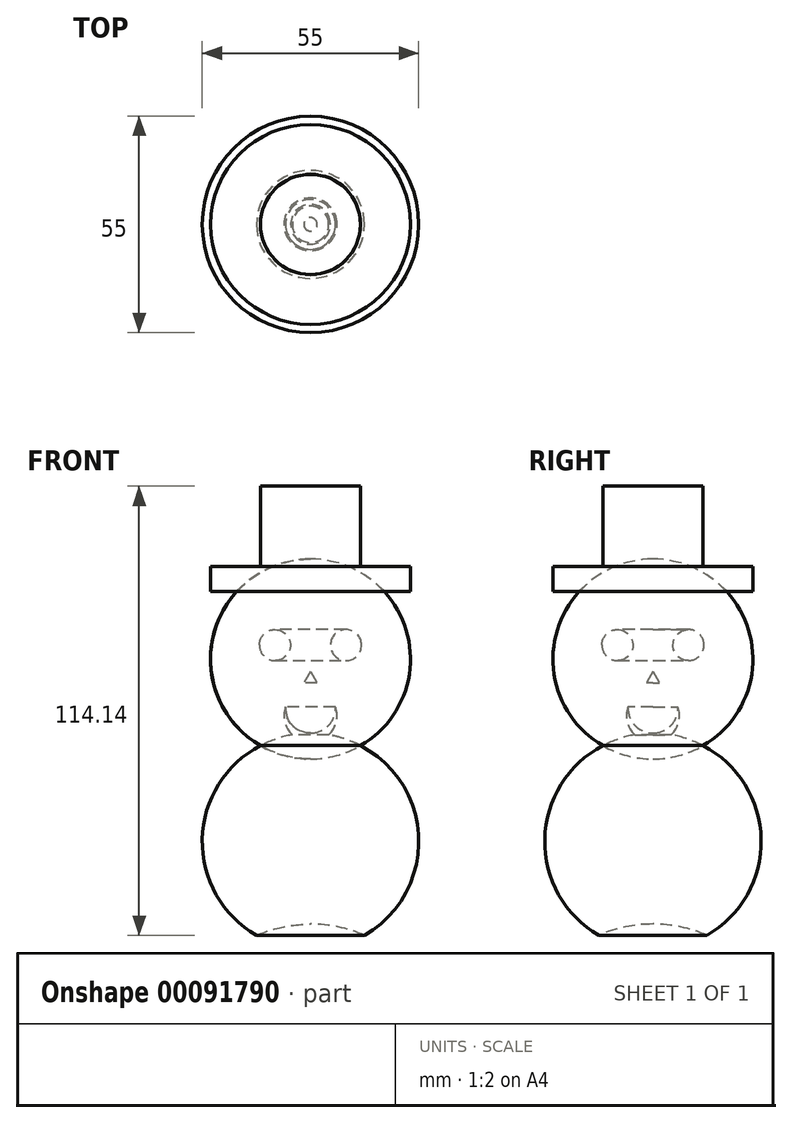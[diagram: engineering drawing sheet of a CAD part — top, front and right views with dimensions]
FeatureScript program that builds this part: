
annotation { "Feature Type Name" : "Feature", "Feature Type Description" : "" }
export const myFeature = defineFeature(function(context is Context, id is Id, definition is map)
    precondition{}
    {
        {
            var Q0;
            Q0=qCreatedBy(makeId("Front.planeOp"),FACE);
            var sketch = newSketch(context, id + "F0", { "sketchPlane" : qUnion([Q0])});
            skCircle(sketch, "E0", {"center": v(0, 0) * mm, "radius": 27.5 * mm});
            skCircle(sketch, "E1", {"center": v(0, 46.37) * mm, "radius": 25.4 * mm});
            skCircle(sketch, "E2", {"center": v(0, -55.26) * mm, "radius": 34.3 * mm});
            skCircle(sketch, "E3", {"center": v(-9.03, 49.92) * mm, "radius": 3.95 * mm});
            skCircle(sketch, "E4.MirrorC", {"center": v(9.03, 49.92) * mm, "radius": 3.95 * mm});
            skLineSegment(sketch, "E5", {"start": v(0, 43.2) * mm, "end": v(-1.7, 40.25) * mm});
            skLineSegment(sketch, "E6", {"start": v(-1.7, 40.25) * mm, "end": v(1.7, 40.25) * mm});
            skPoint(sketch, "E7.endSnap0", {"position": v(-0.85, 41.73) * mm});
            skLineSegment(sketch, "E8", {"start": v(0, 43.2) * mm, "end": v(1.7, 40.25) * mm});
            skArc(sketch, "E9", {"start": v(-6.34, 34.24) * mm, "mid": v(-4.6, 29.53) * mm, "end": v(0, 27.55) * mm});
            skArc(sketch, "E10", {"start": v(-6.34, 34.24) * mm, "mid": v(-5.5, 28.11) * mm, "end": v(0, 25.27) * mm});
            skArc(sketch, "E11.MirrorCS", {"start": v(6.34, 34.24) * mm, "mid": v(4.6, 29.53) * mm, "end": v(0, 27.55) * mm});
            skArc(sketch, "E12.MirrorCS", {"start": v(6.34, 34.24) * mm, "mid": v(5.5, 28.11) * mm, "end": v(0, 25.27) * mm});
            skLineSegment(sketch, "E13", {"start": v(0, 71.77) * mm, "end": v(0, -89.55) * mm});
            skSolve(sketch);
        }
        {
            var Q0;
            Q0=qCreatedBy(makeId("Front.planeOp"),FACE);
            var sketch = newSketch(context, id + "F1", { "sketchPlane" : qUnion([Q0])});
            skLineSegment(sketch, "E14.bottom", {"start": v(0, 69.85) * mm, "end": v(25.4, 69.85) * mm});
            skLineSegment(sketch, "E14.top", {"start": v(0, 63.5) * mm, "end": v(25.4, 63.5) * mm});
            skLineSegment(sketch, "E14.left", {"start": v(0, 69.85) * mm, "end": v(0, 63.5) * mm});
            skLineSegment(sketch, "E14.right", {"start": v(25.4, 69.85) * mm, "end": v(25.4, 63.5) * mm});
            skLineSegment(sketch, "E15.top", {"start": v(12.7, 90.3) * mm, "end": v(0, 90.3) * mm});
            skLineSegment(sketch, "E15.left", {"start": v(12.7, 69.85) * mm, "end": v(12.7, 90.3) * mm});
            skLineSegment(sketch, "E15.right", {"start": v(0, 69.85) * mm, "end": v(0, 90.3) * mm});
            skLineSegment(sketch, "E16.MirrorCS", {"start": v(-12.7, 90.3) * mm, "end": v(0, 90.3) * mm});
            skLineSegment(sketch, "E17.MirrorCS", {"start": v(-12.7, 69.85) * mm, "end": v(-12.7, 90.3) * mm});
            skLineSegment(sketch, "E18.MirrorCS", {"start": v(0, 63.5) * mm, "end": v(-25.4, 63.5) * mm});
            skLineSegment(sketch, "E19.MirrorCS", {"start": v(-25.4, 69.85) * mm, "end": v(-25.4, 63.5) * mm});
            skLineSegment(sketch, "E20.MirrorCS", {"start": v(0, 69.85) * mm, "end": v(-25.4, 69.85) * mm});
            skSolve(sketch);
        }
        {
            var Q0;
            Q0=makeQuery(id+"F0.imprint","IMPRINT",FACE,{"disambiguationData":[TD([[makeQuery(id+"F0.imprint","IMPRINT",EDGE,{"derivedFrom":sQuery(id+"F0.wireOp",EDGE,"E3")}),-1.0]])]});
            var Q1;
            {var subQ0=sQuery(id+"F0.wireOp",EDGE,"E1");var subQ1=sQuery(id+"F0.wireOp",EDGE,"E0");var subQ2=makeQuery(id+"F0.imprint","INTERSECT",VERTEX,{"disambiguationData":[OD(1.0)],"derivedFrom":[subQ1,subQ0]});Q1=makeQuery(id+"F0.imprint","IMPRINT",FACE,{"disambiguationData":[TD([[makeQuery(id+"F0.imprint","IMPRINT",EDGE,{"disambiguationData":[TD([[subQ2,-1.0]])],"derivedFrom":subQ1}),1.0]])]});}
            var Q2;
            {var subQ0=sQuery(id+"F0.wireOp",EDGE,"E2");var subQ1=sQuery(id+"F0.wireOp",EDGE,"E0");var subQ2=makeQuery(id+"F0.imprint","INTERSECT",VERTEX,{"disambiguationData":[OD(0.0)],"derivedFrom":[subQ1,subQ0]});Q2=makeQuery(id+"F0.imprint","IMPRINT",FACE,{"disambiguationData":[TD([[makeQuery(id+"F0.imprint","IMPRINT",EDGE,{"disambiguationData":[TD([[subQ2,-1.0]])],"derivedFrom":subQ1}),-1.0]])]});}
            var Q3;
            Q3=sQuery(id+"F0.wireOp",EDGE,"E3");
            var Q4;
            Q4=sQuery(id+"F0.wireOp",EDGE,"E1");
            var Q5;
            Q5=sQuery(id+"F0.wireOp",EDGE,"E0");
            var Q6;
            Q6=sQuery(id+"F0.wireOp",EDGE,"E10");
            var Q7;
            Q7=sQuery(id+"F0.wireOp",EDGE,"E9");
            var Q8;
            Q8=sQuery(id+"F0.wireOp",EDGE,"E5");
            var Q9;
            Q9=sQuery(id+"F0.wireOp",EDGE,"E6");
            var Q10;
            Q10=sQuery(id+"F0.wireOp",EDGE,"E2");
            var Q11;
            Q11=sQuery(id+"F0.wireOp",EDGE,"E13");
            revolve(context, id + "F2", {"entities" : qUnion([Q0, Q1, Q2]), "surfaceEntities" : qUnion([Q3, Q4, Q5, Q6, Q7, Q8, Q9, Q10]), "axis" : qUnion([Q11]), "revolveType" : RevolveType.FULL});
        }
        {
            var Q0;
            {var subQ0=sQuery(id+"F1.wireOp",EDGE,"E15.right");Q0=makeQuery(id+"F1.imprint","IMPRINT",FACE,{"disambiguationData":[TD([[makeQuery(id+"F1.imprint","IMPRINT",EDGE,{"derivedFrom":subQ0}),1.0]])]});}
            var Q1;
            {var subQ1=sQuery(id+"F1.wireOp",EDGE,"E14.left");Q1=makeQuery(id+"F1.imprint","IMPRINT",FACE,{"disambiguationData":[TD([[makeQuery(id+"F1.imprint","IMPRINT",EDGE,{"derivedFrom":subQ1}),-1.0]])]});}
            var Q2;
            Q2=sQuery(id+"F1.wireOp",EDGE,"E17.MirrorCS");
            var Q3;
            Q3=sQuery(id+"F1.wireOp",EDGE,"E20.MirrorCS");
            var Q4;
            Q4=sQuery(id+"F1.wireOp",EDGE,"E19.MirrorCS");
            var Q5;
            Q5=sQuery(id+"F1.wireOp",EDGE,"E18.MirrorCS");
            var Q6;
            Q6=sQuery(id+"F1.wireOp",EDGE,"E16.MirrorCS");
            var Q7;
            Q7=sQuery(id+"F1.wireOp",EDGE,"E14.left");
            revolve(context, id + "F3", {"entities" : qUnion([Q0, Q1]), "surfaceEntities" : qUnion([Q2, Q3, Q4, Q5, Q6]), "axis" : qUnion([Q7]), "revolveType" : RevolveType.FULL});
        }
        {
            var Q0;
            Q0=sQuery(id+"F0.wireOp",EDGE,"E3");
            var Q1;
            Q1=sQuery(id+"F0.wireOp",EDGE,"E4.MirrorC");
            var Q2;
            Q2=sQuery(id+"F0.wireOp",EDGE,"E5");
            var Q3;
            Q3=sQuery(id+"F0.wireOp",EDGE,"E8");
            var Q4;
            Q4=sQuery(id+"F0.wireOp",EDGE,"E6");
            var Q5;
            Q5=sQuery(id+"F0.wireOp",EDGE,"E9");
            var Q6;
            Q6=sQuery(id+"F0.wireOp",EDGE,"E10");
            var Q7;
            Q7=sQuery(id+"F0.wireOp",EDGE,"E11.MirrorCS");
            var Q8;
            Q8=sQuery(id+"F0.wireOp",EDGE,"E12.MirrorCS");
            extrude(context, id + "F4", {"bodyType" : ToolBodyType.SURFACE, "operationType" : NewBodyOperationType.REMOVE, "surfaceEntities" : qUnion([Q0, Q1, Q2, Q3, Q4, Q5, Q6, Q7, Q8]), "oppositeDirection" : true, "depth" : 25.4 * mm});
        }
    });
